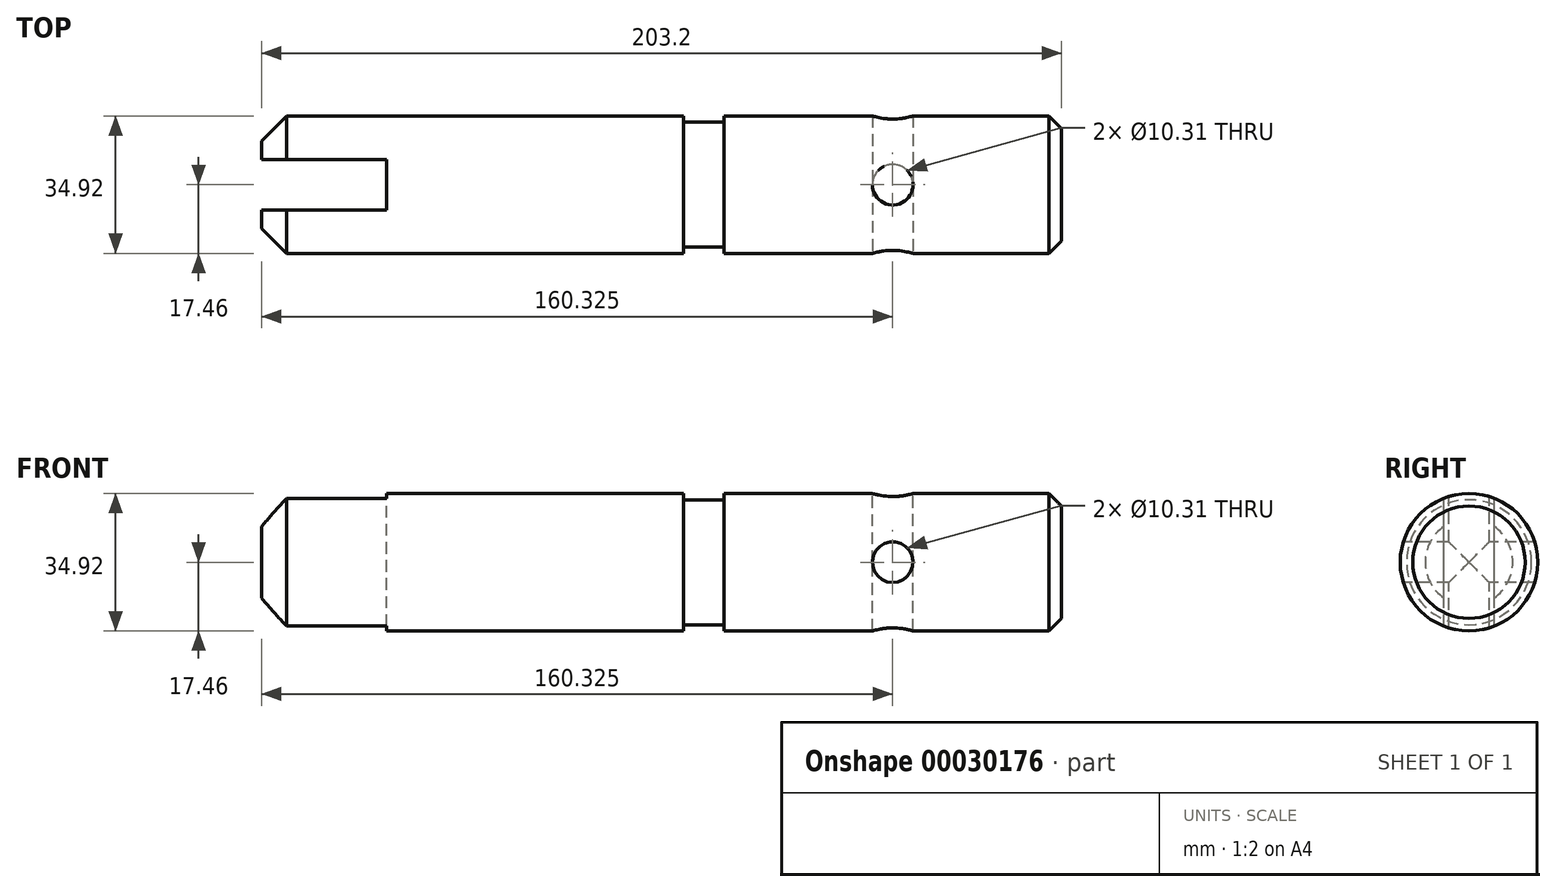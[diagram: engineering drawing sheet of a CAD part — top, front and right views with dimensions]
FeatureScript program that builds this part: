
annotation { "Feature Type Name" : "Feature", "Feature Type Description" : "" }
export const myFeature = defineFeature(function(context is Context, id is Id, definition is map)
    precondition{}
    {
        {
            var Q0;
            Q0=qCreatedBy(makeId("Top.planeOp"),FACE);
            var sketch = newSketch(context, id + "F0", { "sketchPlane" : qUnion([Q0])});
            skLineSegment(sketch, "E0.bottom", {"start": v(0, 0) * mm, "end": v(-203.2, 0) * mm});
            skLineSegment(sketch, "E0.top", {"start": v(0, 17.46) * mm, "end": v(-85.73, 17.46) * mm});
            skLineSegment(sketch, "E0.left", {"start": v(0, 0) * mm, "end": v(0, 17.46) * mm});
            skLineSegment(sketch, "E0.right", {"start": v(-203.2, 0) * mm, "end": v(-203.2, 17.46) * mm});
            skLineSegment(sketch, "E1", {"start": v(-247.25, 0) * mm, "end": v(82.56, 0) * mm, "construction": true});
            skLineSegment(sketch, "E2.0", {"start": v(-85.73, 15.87) * mm, "end": v(-85.73, 17.46) * mm});
            skLineSegment(sketch, "E3.0", {"start": v(-96.04, 15.87) * mm, "end": v(-96.04, 17.46) * mm});
            skLineSegment(sketch, "E4.0", {"start": v(-85.73, 15.87) * mm, "end": v(-96.04, 15.87) * mm});
            skLineSegment(sketch, "E5.trimOffspring", {"start": v(-96.04, 17.46) * mm, "end": v(-203.2, 17.46) * mm});
            skSolve(sketch);
        }
        {
            var Q0;
            Q0 = qSketchRegion(id + "F0", true);
            var Q1;
            Q1=sQuery(id+"F0.wireOp",EDGE,"E1");
            revolve(context, id + "F1", {"entities" : qUnion([Q0]), "axis" : qUnion([Q1]), "revolveType" : RevolveType.FULL});
        }
        {
            var Q0;
            Q0=makeQuery(id+"F1.opRevolve","SWEPT_EDGE",EDGE,{"disambiguationData":[OSD([sQuery(id+"F0.wireOp",EDGE,"E0.right"),sQuery(id+"F0.wireOp",EDGE,"E5.trimOffspring")])]});
            chamfer(context, id + "F2", {"entities" : qUnion([Q0]), "width" : 6.35 * mm, "tangentPropagation" : true});
        }
        {
            var Q0;
            Q0=makeQuery(id+"F1.opRevolve","SWEPT_EDGE",EDGE,{"disambiguationData":[OSD([sQuery(id+"F0.wireOp",EDGE,"E0.top"),sQuery(id+"F0.wireOp",EDGE,"E0.left")])]});
            chamfer(context, id + "F3", {"entities" : qUnion([Q0]), "width" : 3.17 * mm, "tangentPropagation" : true});
        }
        {
            var Q0;
            Q0=qCreatedBy(makeId("Top.planeOp"),FACE);
            var sketch = newSketch(context, id + "F4", { "sketchPlane" : qUnion([Q0])});
            skLineSegment(sketch, "E6.bottom", {"start": v(-204.47, 6.41) * mm, "end": v(-171.45, 6.41) * mm});
            skLineSegment(sketch, "E6.top", {"start": v(-204.47, -6.41) * mm, "end": v(-171.45, -6.41) * mm});
            skLineSegment(sketch, "E6.left", {"start": v(-204.47, 6.41) * mm, "end": v(-204.47, -6.41) * mm});
            skLineSegment(sketch, "E6.right", {"start": v(-171.45, 6.41) * mm, "end": v(-171.45, -6.41) * mm});
            skCircle(sketch, "E7", {"center": v(-42.88, 0) * mm, "radius": 5.16 * mm});
            skSolve(sketch);
        }
        {
            var Q0;
            Q0 = qSketchRegion(id + "F4", true);
            extrude(context, id + "F5", {"entities" : qUnion([Q0]), "operationType" : NewBodyOperationType.REMOVE, "endBound" : BoundingType.SYMMETRIC, "oppositeDirection" : true, "depth" : 38.1 * mm});
        }
        {
            var Q0;
            Q0=qCreatedBy(makeId("Front.planeOp"),FACE);
            var sketch = newSketch(context, id + "F6", { "sketchPlane" : qUnion([Q0])});
            skCircle(sketch, "E8", {"center": v(-42.88, 0) * mm, "radius": 5.16 * mm});
            skSolve(sketch);
        }
        {
            var Q0;
            Q0 = qSketchRegion(id + "F6", true);
            extrude(context, id + "F7", {"entities" : qUnion([Q0]), "operationType" : NewBodyOperationType.REMOVE, "endBound" : BoundingType.SYMMETRIC, "oppositeDirection" : true, "depth" : 38.1 * mm});
        }
    });
